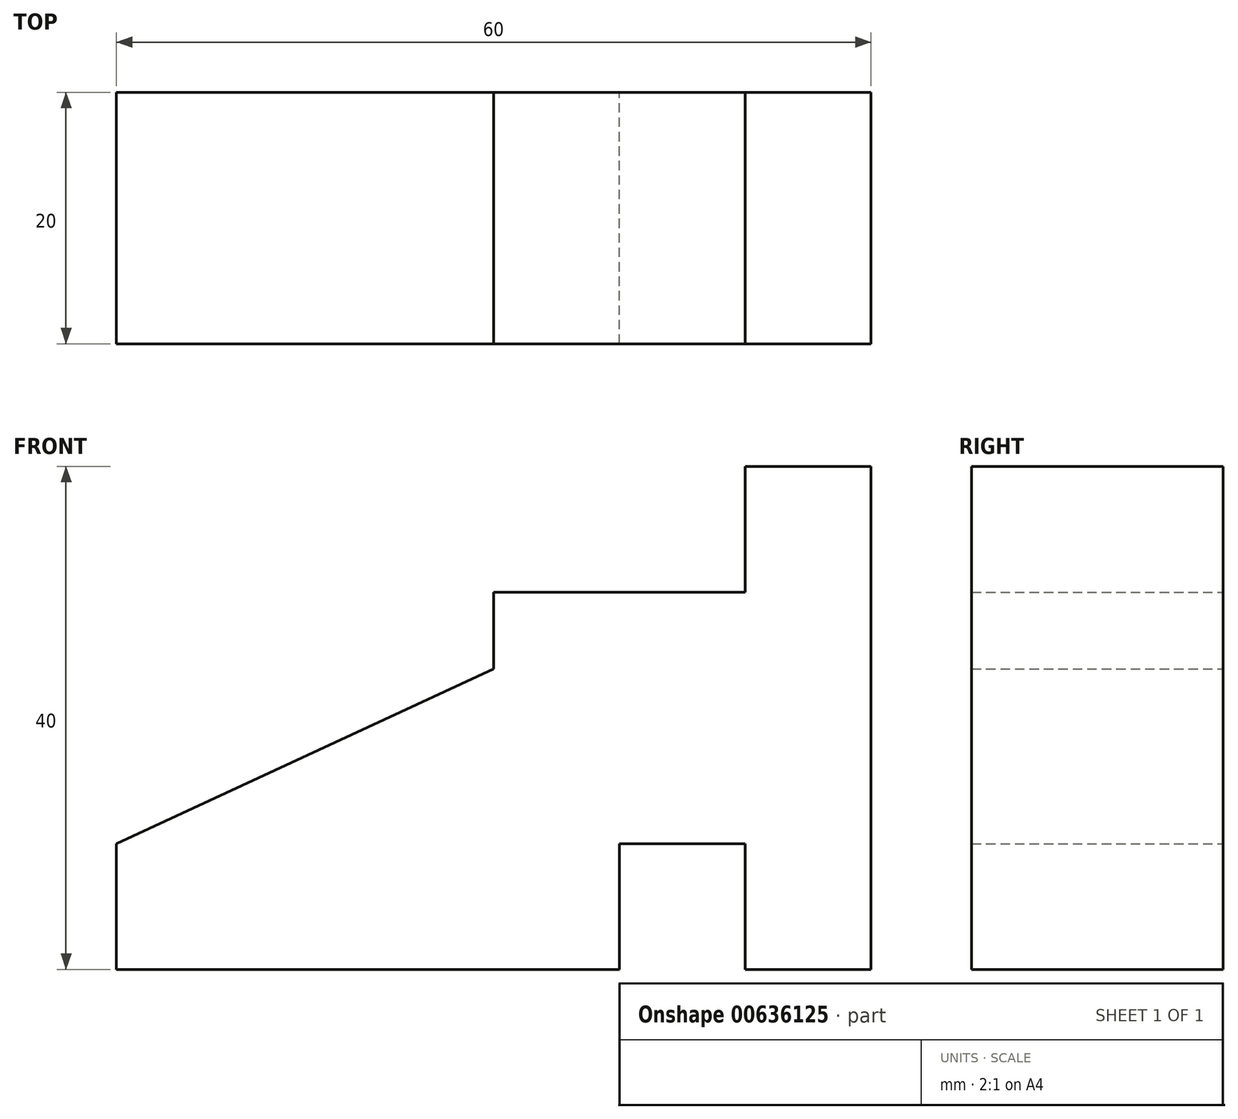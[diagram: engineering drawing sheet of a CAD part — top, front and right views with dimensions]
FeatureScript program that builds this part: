
annotation { "Feature Type Name" : "Feature", "Feature Type Description" : "" }
export const myFeature = defineFeature(function(context is Context, id is Id, definition is map)
    precondition{}
    {
        {
            var Q0;
            Q0=qCreatedBy(makeId("Front.planeOp"),FACE);
            var sketch = newSketch(context, id + "F0", { "sketchPlane" : qUnion([Q0])});
            skLineSegment(sketch, "E0", {"start": v(12.49, -15.1) * mm, "end": v(12.49, -5.1) * mm});
            skLineSegment(sketch, "E1", {"start": v(12.49, -5.1) * mm, "end": v(22.49, -5.1) * mm});
            skLineSegment(sketch, "E2", {"start": v(22.49, -5.1) * mm, "end": v(22.49, -15.1) * mm});
            skLineSegment(sketch, "E3", {"start": v(22.49, -15.1) * mm, "end": v(32.49, -15.1) * mm});
            skLineSegment(sketch, "E4", {"start": v(32.49, -15.1) * mm, "end": v(32.49, 24.9) * mm});
            skLineSegment(sketch, "E5", {"start": v(32.49, 24.9) * mm, "end": v(22.49, 24.9) * mm});
            skLineSegment(sketch, "E6", {"start": v(22.49, 24.9) * mm, "end": v(22.49, 14.9) * mm});
            skLineSegment(sketch, "E7", {"start": v(22.49, 14.9) * mm, "end": v(2.49, 14.9) * mm});
            skLineSegment(sketch, "E8", {"start": v(2.49, 14.9) * mm, "end": v(2.49, 8.8) * mm});
            skLineSegment(sketch, "E9", {"start": v(2.49, 8.8) * mm, "end": v(-27.51, -5.1) * mm});
            skLineSegment(sketch, "E10", {"start": v(-27.51, -5.1) * mm, "end": v(-27.51, -15.1) * mm});
            skLineSegment(sketch, "E11", {"start": v(-27.51, -15.1) * mm, "end": v(12.49, -15.1) * mm});
            skSolve(sketch);
        }
        {
            var Q0;
            Q0 = qSketchRegion(id + "F0", true);
            extrude(context, id + "F1", {"entities" : qUnion([Q0]), "depth" : 20 * mm, "offsetDistance" : 25 * mm});
        }
    });
